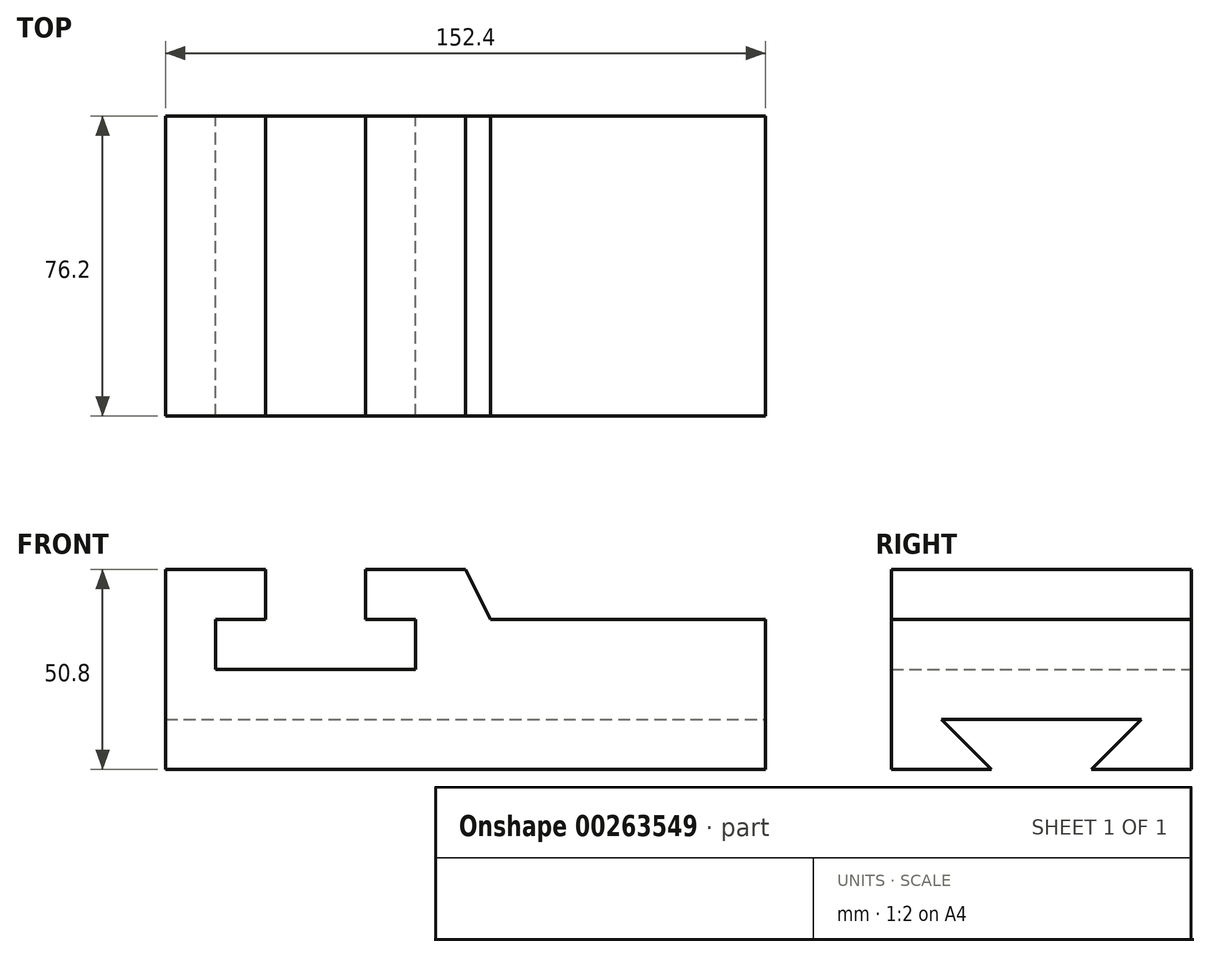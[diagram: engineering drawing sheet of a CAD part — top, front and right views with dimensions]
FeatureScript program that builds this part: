
annotation { "Feature Type Name" : "Feature", "Feature Type Description" : "" }
export const myFeature = defineFeature(function(context is Context, id is Id, definition is map)
    precondition{}
    {
        {
            var Q0;
            Q0=qCreatedBy(makeId("Front.planeOp"),FACE);
            var sketch = newSketch(context, id + "F0", { "sketchPlane" : qUnion([Q0])});
            skLineSegment(sketch, "E0", {"start": v(-63.5, 12.7) * mm, "end": v(-63.5, -38.1) * mm});
            skLineSegment(sketch, "E1", {"start": v(-63.5, -38.1) * mm, "end": v(88.9, -38.1) * mm});
            skLineSegment(sketch, "E2", {"start": v(-63.5, 12.7) * mm, "end": v(-38.1, 12.7) * mm});
            skLineSegment(sketch, "E3", {"start": v(-38.1, 12.7) * mm, "end": v(-38.1, 0) * mm});
            skLineSegment(sketch, "E4", {"start": v(-38.1, 0) * mm, "end": v(-50.8, 0) * mm});
            skLineSegment(sketch, "E5", {"start": v(-50.8, 0) * mm, "end": v(-50.8, -12.7) * mm});
            skLineSegment(sketch, "E6", {"start": v(-50.8, -12.7) * mm, "end": v(0, -12.7) * mm});
            skLineSegment(sketch, "E7", {"start": v(0, -12.7) * mm, "end": v(0, 0) * mm});
            skLineSegment(sketch, "E8", {"start": v(0, 0) * mm, "end": v(-12.7, 0) * mm});
            skLineSegment(sketch, "E9", {"start": v(-12.7, 0) * mm, "end": v(-12.7, 12.7) * mm});
            skLineSegment(sketch, "E10", {"start": v(-12.7, 12.7) * mm, "end": v(12.7, 12.7) * mm});
            skLineSegment(sketch, "E11", {"start": v(88.9, -38.1) * mm, "end": v(88.9, 0) * mm});
            skLineSegment(sketch, "E12", {"start": v(88.9, 0) * mm, "end": v(19.05, 0) * mm});
            skLineSegment(sketch, "E13", {"start": v(12.7, 12.7) * mm, "end": v(19.05, 0) * mm});
            skSolve(sketch);
        }
        {
            var Q0;
            Q0=makeQuery(id+"F0.imprint","IMPRINT",FACE,{"disambiguationData":[TD([[makeQuery(id+"F0.imprint","IMPRINT",EDGE,{"derivedFrom":sQuery(id+"F0.wireOp",EDGE,"E0")}),1.0]])]});
            extrude(context, id + "F1", {"entities" : qUnion([Q0]), "depth" : 76.2 * mm});
        }
        {
            var Q0;
            Q0=makeQuery(id+"F1.opExtrude","SWEPT_FACE",FACE,{"disambiguationData":[OSD([sQuery(id+"F0.wireOp",EDGE,"E11")])]});
            var sketch = newSketch(context, id + "F2", { "sketchPlane" : qUnion([Q0])});
            skLineSegment(sketch, "E14", {"start": v(-76.2, -38.1) * mm, "end": v(-50.8, -38.1) * mm});
            skLineSegment(sketch, "E15", {"start": v(0, -38.1) * mm, "end": v(-25.4, -38.1) * mm});
            skLineSegment(sketch, "E16", {"start": v(-12.7, -25.4) * mm, "end": v(-63.5, -25.4) * mm});
            skLineSegment(sketch, "E17", {"start": v(-50.8, -38.1) * mm, "end": v(-63.5, -25.4) * mm});
            skLineSegment(sketch, "E18", {"start": v(-25.4, -38.1) * mm, "end": v(-12.7, -25.4) * mm});
            skSolve(sketch);
        }
        {
            var Q0;
            Q0 = qSketchRegion(id + "F2", true);
            var Q1;
            Q1=makeQuery(id+"F2.imprint","IMPRINT",FACE,{"disambiguationData":[TD([[makeQuery(id+"F2.imprint","IMPRINT",EDGE,{"derivedFrom":sQuery(id+"F2.wireOp",EDGE,"E16")}),1.0]])]});
            extrude(context, id + "F3", {"entities" : qUnion([Q0, Q1]), "operationType" : NewBodyOperationType.REMOVE, "oppositeDirection" : true, "depth" : 152.4 * mm});
        }
    });
